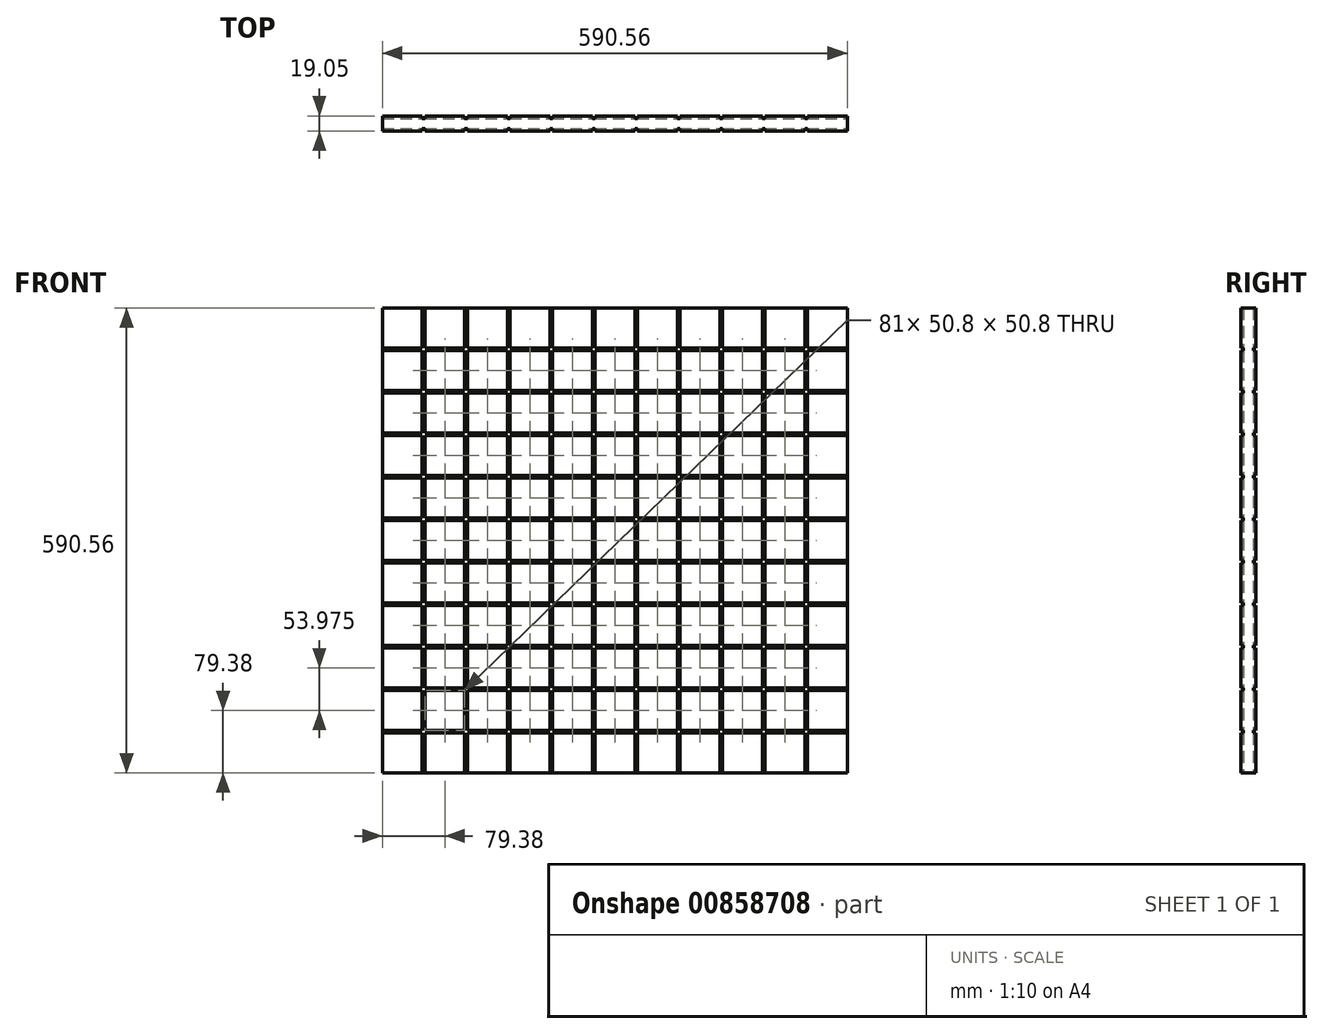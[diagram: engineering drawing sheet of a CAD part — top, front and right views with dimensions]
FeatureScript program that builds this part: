
annotation { "Feature Type Name" : "Feature", "Feature Type Description" : "" }
export const myFeature = defineFeature(function(context is Context, id is Id, definition is map)
    precondition{}
    {
        {
            var Q0;
            Q0=qCreatedBy(makeId("Front.planeOp"),FACE);
            var sketch = newSketch(context, id + "F0", { "sketchPlane" : qUnion([Q0])});
            skLineSegment(sketch, "E0.bottom", {"start": v(295.27, 295.28) * mm, "end": v(-295.27, 295.28) * mm});
            skLineSegment(sketch, "E0.top", {"start": v(295.27, -295.28) * mm, "end": v(-295.27, -295.28) * mm});
            skLineSegment(sketch, "E0.left", {"start": v(295.28, 295.27) * mm, "end": v(295.28, -295.28) * mm});
            skLineSegment(sketch, "E0.right", {"start": v(-295.28, 295.27) * mm, "end": v(-295.28, -295.27) * mm});
            skPoint(sketch, "E0.middle", {"position": v(0, 0) * mm});
            skSolve(sketch);
        }
        {
            var Q0;
            Q0=makeQuery(id+"F0.imprint","IMPRINT",FACE,{"disambiguationData":[TD([[makeQuery(id+"F0.imprint","IMPRINT",EDGE,{"derivedFrom":sQuery(id+"F0.wireOp",EDGE,"E0.bottom")}),1.0]])]});
            extrude(context, id + "F1", {"entities" : qUnion([Q0]), "depth" : 19.05 * mm, "offsetDistance" : 25.4 * mm});
        }
        {
            var Q0;
            Q0=makeQuery(id+"F1.opExtrude","CAP_FACE",FACE,{"disambiguationData":[OSD([sQuery(id+"F0.wireOp",EDGE,"E0.bottom"),sQuery(id+"F0.wireOp",EDGE,"E0.top"),sQuery(id+"F0.wireOp",EDGE,"E0.left"),sQuery(id+"F0.wireOp",EDGE,"E0.right")])],"isStart":false});
            var sketch = newSketch(context, id + "F2", { "sketchPlane" : qUnion([Q0])});
            skLineSegment(sketch, "E1.bottom", {"start": v(-244.48, 295.28) * mm, "end": v(-241.3, 295.28) * mm});
            skLineSegment(sketch, "E1.top", {"start": v(-244.47, -295.28) * mm, "end": v(-241.3, -295.28) * mm});
            skLineSegment(sketch, "E1.left", {"start": v(-244.48, 295.28) * mm, "end": v(-244.47, -295.28) * mm});
            skLineSegment(sketch, "E1.right", {"start": v(-241.3, 295.28) * mm, "end": v(-241.3, -295.28) * mm});
            skLineSegment(sketch, "E2.1.0.0", {"start": v(-190.5, 295.28) * mm, "end": v(-190.5, -295.28) * mm});
            skLineSegment(sketch, "E2.1.0.1", {"start": v(-187.32, 295.28) * mm, "end": v(-187.32, -295.28) * mm});
            skLineSegment(sketch, "E2.1.0.2", {"start": v(-190.5, 295.28) * mm, "end": v(-187.32, 295.28) * mm});
            skLineSegment(sketch, "E2.2.0.0", {"start": v(-136.52, 295.28) * mm, "end": v(-136.53, -295.28) * mm});
            skLineSegment(sketch, "E2.2.0.1", {"start": v(-133.35, 295.28) * mm, "end": v(-133.35, -295.28) * mm});
            skLineSegment(sketch, "E2.2.0.2", {"start": v(-136.52, 295.28) * mm, "end": v(-133.35, 295.28) * mm});
            skLineSegment(sketch, "E2.direction1", {"start": v(-244.47, -295.28) * mm, "end": v(-190.5, -295.28) * mm, "construction": true});
            skLineSegment(sketch, "E3.1.0.0", {"start": v(-190.5, -295.28) * mm, "end": v(-187.32, -295.28) * mm});
            skLineSegment(sketch, "E3.2.0.0", {"start": v(-136.52, -295.28) * mm, "end": v(-133.35, -295.28) * mm});
            skLineSegment(sketch, "E4.0.3.0", {"start": v(-82.55, -295.28) * mm, "end": v(-79.38, -295.28) * mm});
            skLineSegment(sketch, "E4.0.4.0", {"start": v(-28.57, -295.28) * mm, "end": v(-25.4, -295.28) * mm});
            skLineSegment(sketch, "E4.0.5.0", {"start": v(25.4, -295.28) * mm, "end": v(28.57, -295.28) * mm});
            skLineSegment(sketch, "E4.0.6.0", {"start": v(79.38, -295.28) * mm, "end": v(82.55, -295.28) * mm});
            skLineSegment(sketch, "E4.0.7.0", {"start": v(133.35, -295.28) * mm, "end": v(136.52, -295.28) * mm});
            skLineSegment(sketch, "E4.0.8.0", {"start": v(187.32, -295.28) * mm, "end": v(190.5, -295.28) * mm});
            skLineSegment(sketch, "E4.0.9.0", {"start": v(241.3, -295.28) * mm, "end": v(244.47, -295.28) * mm});
            skLineSegment(sketch, "E5.0.3.0", {"start": v(-82.55, 295.28) * mm, "end": v(-82.55, -295.28) * mm});
            skLineSegment(sketch, "E5.3.3.0", {"start": v(-79.37, 295.28) * mm, "end": v(-79.37, -295.28) * mm});
            skLineSegment(sketch, "E5.6.3.0", {"start": v(-82.55, 295.28) * mm, "end": v(-79.37, 295.28) * mm});
            skLineSegment(sketch, "E5.0.4.0", {"start": v(-28.57, 295.28) * mm, "end": v(-28.57, -295.28) * mm});
            skLineSegment(sketch, "E5.3.4.0", {"start": v(-25.4, 295.28) * mm, "end": v(-25.4, -295.28) * mm});
            skLineSegment(sketch, "E5.6.4.0", {"start": v(-28.57, 295.28) * mm, "end": v(-25.4, 295.28) * mm});
            skLineSegment(sketch, "E5.0.5.0", {"start": v(25.4, 295.28) * mm, "end": v(25.4, -295.28) * mm});
            skLineSegment(sketch, "E5.3.5.0", {"start": v(28.58, 295.28) * mm, "end": v(28.58, -295.28) * mm});
            skLineSegment(sketch, "E5.6.5.0", {"start": v(25.4, 295.28) * mm, "end": v(28.58, 295.28) * mm});
            skLineSegment(sketch, "E5.0.6.0", {"start": v(79.38, 295.28) * mm, "end": v(79.38, -295.28) * mm});
            skLineSegment(sketch, "E5.3.6.0", {"start": v(82.55, 295.28) * mm, "end": v(82.55, -295.28) * mm});
            skLineSegment(sketch, "E5.6.6.0", {"start": v(79.38, 295.28) * mm, "end": v(82.55, 295.28) * mm});
            skLineSegment(sketch, "E5.0.7.0", {"start": v(133.35, 295.28) * mm, "end": v(133.35, -295.28) * mm});
            skLineSegment(sketch, "E5.3.7.0", {"start": v(136.53, 295.28) * mm, "end": v(136.53, -295.28) * mm});
            skLineSegment(sketch, "E5.6.7.0", {"start": v(133.35, 295.28) * mm, "end": v(136.53, 295.28) * mm});
            skLineSegment(sketch, "E5.0.8.0", {"start": v(187.33, 295.28) * mm, "end": v(187.33, -295.28) * mm});
            skLineSegment(sketch, "E5.3.8.0", {"start": v(190.5, 295.28) * mm, "end": v(190.5, -295.28) * mm});
            skLineSegment(sketch, "E5.6.8.0", {"start": v(187.33, 295.28) * mm, "end": v(190.5, 295.28) * mm});
            skLineSegment(sketch, "E5.0.9.0", {"start": v(241.3, 295.28) * mm, "end": v(241.3, -295.28) * mm});
            skLineSegment(sketch, "E5.3.9.0", {"start": v(244.48, 295.28) * mm, "end": v(244.48, -295.28) * mm});
            skLineSegment(sketch, "E5.6.9.0", {"start": v(241.3, 295.28) * mm, "end": v(244.48, 295.28) * mm});
            skSolve(sketch);
        }
        {
            var Q0;
            Q0=qSketchRegion(id+"F2",true);
            extrude(context, id + "F3", {"entities" : qUnion([Q0]), "operationType" : NewBodyOperationType.REMOVE, "oppositeDirection" : true, "depth" : 3.17 * mm, "offsetDistance" : 25.4 * mm});
        }
        {
            var Q0;
            {var subQ0=sQuery(id+"F0.wireOp",EDGE,"E0.bottom");var subQ1=sQuery(id+"F0.wireOp",EDGE,"E0.right");var subQ2=sQuery(id+"F0.wireOp",EDGE,"E0.top");Q0=makeQuery(id+"F3.boolean.opBoolean","SPLIT",FACE,{"disambiguationData":[TD([makeQuery(id+"F1.opExtrude","SWEPT_FACE",FACE,{"disambiguationData":[OSD([subQ1])]})])],"derivedFrom":makeQuery(id+"F1.opExtrude","CAP_FACE",FACE,{"disambiguationData":[OSD([subQ0,subQ2,sQuery(id+"F0.wireOp",EDGE,"E0.left"),subQ1])],"isStart":false})});}
            var sketch = newSketch(context, id + "F4", { "sketchPlane" : qUnion([Q0])});
            skLineSegment(sketch, "E6.bottom", {"start": v(-295.27, 244.47) * mm, "end": v(295.28, 244.47) * mm});
            skLineSegment(sketch, "E6.top", {"start": v(-295.27, 241.3) * mm, "end": v(295.28, 241.3) * mm});
            skLineSegment(sketch, "E6.left", {"start": v(-295.28, 244.47) * mm, "end": v(-295.28, 241.3) * mm});
            skLineSegment(sketch, "E6.right", {"start": v(295.28, 244.47) * mm, "end": v(295.28, 241.3) * mm});
            skLineSegment(sketch, "E7.0.1.0", {"start": v(-295.28, 190.5) * mm, "end": v(-295.28, 187.33) * mm});
            skLineSegment(sketch, "E7.0.1.1", {"start": v(-295.27, 190.5) * mm, "end": v(295.28, 190.5) * mm});
            skLineSegment(sketch, "E7.0.1.2", {"start": v(-295.27, 187.32) * mm, "end": v(295.28, 187.32) * mm});
            skLineSegment(sketch, "E7.0.1.3", {"start": v(295.28, 190.5) * mm, "end": v(295.28, 187.32) * mm});
            skLineSegment(sketch, "E7.0.2.0", {"start": v(-295.28, 136.53) * mm, "end": v(-295.28, 133.35) * mm});
            skLineSegment(sketch, "E7.0.2.1", {"start": v(-295.27, 136.53) * mm, "end": v(295.28, 136.53) * mm});
            skLineSegment(sketch, "E7.0.2.2", {"start": v(-295.27, 133.35) * mm, "end": v(295.28, 133.35) * mm});
            skLineSegment(sketch, "E7.0.2.3", {"start": v(295.28, 136.53) * mm, "end": v(295.28, 133.35) * mm});
            skLineSegment(sketch, "E7.0.3.0", {"start": v(-295.28, 82.55) * mm, "end": v(-295.28, 79.38) * mm});
            skLineSegment(sketch, "E7.0.3.1", {"start": v(-295.27, 82.55) * mm, "end": v(295.28, 82.55) * mm});
            skLineSegment(sketch, "E7.0.3.2", {"start": v(-295.27, 79.38) * mm, "end": v(295.28, 79.38) * mm});
            skLineSegment(sketch, "E7.0.3.3", {"start": v(295.28, 82.55) * mm, "end": v(295.28, 79.38) * mm});
            skLineSegment(sketch, "E7.0.4.0", {"start": v(-295.28, 28.58) * mm, "end": v(-295.28, 25.4) * mm});
            skLineSegment(sketch, "E7.0.4.1", {"start": v(-295.27, 28.58) * mm, "end": v(295.28, 28.58) * mm});
            skLineSegment(sketch, "E7.0.4.2", {"start": v(-295.27, 25.4) * mm, "end": v(295.28, 25.4) * mm});
            skLineSegment(sketch, "E7.0.4.3", {"start": v(295.28, 28.58) * mm, "end": v(295.28, 25.4) * mm});
            skLineSegment(sketch, "E7.0.5.0", {"start": v(-295.28, -25.4) * mm, "end": v(-295.28, -28.57) * mm});
            skLineSegment(sketch, "E7.0.5.1", {"start": v(-295.27, -25.4) * mm, "end": v(295.28, -25.4) * mm});
            skLineSegment(sketch, "E7.0.5.2", {"start": v(-295.27, -28.57) * mm, "end": v(295.28, -28.57) * mm});
            skLineSegment(sketch, "E7.0.5.3", {"start": v(295.28, -25.4) * mm, "end": v(295.28, -28.57) * mm});
            skLineSegment(sketch, "E7.0.6.0", {"start": v(-295.28, -79.37) * mm, "end": v(-295.28, -82.55) * mm});
            skLineSegment(sketch, "E7.0.6.1", {"start": v(-295.27, -79.37) * mm, "end": v(295.28, -79.37) * mm});
            skLineSegment(sketch, "E7.0.6.2", {"start": v(-295.27, -82.55) * mm, "end": v(295.28, -82.55) * mm});
            skLineSegment(sketch, "E7.0.6.3", {"start": v(295.28, -79.37) * mm, "end": v(295.28, -82.55) * mm});
            skLineSegment(sketch, "E7.0.7.0", {"start": v(-295.28, -133.35) * mm, "end": v(-295.28, -136.52) * mm});
            skLineSegment(sketch, "E7.0.7.1", {"start": v(-295.27, -133.35) * mm, "end": v(295.28, -133.35) * mm});
            skLineSegment(sketch, "E7.0.7.2", {"start": v(-295.27, -136.52) * mm, "end": v(295.28, -136.52) * mm});
            skLineSegment(sketch, "E7.0.7.3", {"start": v(295.28, -133.35) * mm, "end": v(295.28, -136.52) * mm});
            skLineSegment(sketch, "E7.0.8.0", {"start": v(-295.28, -187.32) * mm, "end": v(-295.28, -190.5) * mm});
            skLineSegment(sketch, "E7.0.8.1", {"start": v(-295.27, -187.32) * mm, "end": v(295.28, -187.32) * mm});
            skLineSegment(sketch, "E7.0.8.2", {"start": v(-295.27, -190.5) * mm, "end": v(295.28, -190.5) * mm});
            skLineSegment(sketch, "E7.0.8.3", {"start": v(295.28, -187.32) * mm, "end": v(295.28, -190.5) * mm});
            skLineSegment(sketch, "E7.0.9.0", {"start": v(-295.28, -241.3) * mm, "end": v(-295.28, -244.47) * mm});
            skLineSegment(sketch, "E7.0.9.1", {"start": v(-295.27, -241.3) * mm, "end": v(295.28, -241.3) * mm});
            skLineSegment(sketch, "E7.0.9.2", {"start": v(-295.27, -244.47) * mm, "end": v(295.28, -244.47) * mm});
            skLineSegment(sketch, "E7.0.9.3", {"start": v(295.28, -241.3) * mm, "end": v(295.28, -244.47) * mm});
            skLineSegment(sketch, "E7.1.1.0", {"start": v(-295.28, 190.5) * mm, "end": v(-295.28, 187.33) * mm});
            skLineSegment(sketch, "E7.1.1.1", {"start": v(-295.27, 190.5) * mm, "end": v(295.28, 190.5) * mm});
            skLineSegment(sketch, "E7.1.1.2", {"start": v(-295.27, 187.32) * mm, "end": v(295.28, 187.32) * mm});
            skLineSegment(sketch, "E7.1.1.3", {"start": v(295.28, 190.5) * mm, "end": v(295.28, 187.32) * mm});
            skLineSegment(sketch, "E7.1.2.0", {"start": v(-295.28, 136.53) * mm, "end": v(-295.28, 133.35) * mm});
            skLineSegment(sketch, "E7.1.2.1", {"start": v(-295.27, 136.53) * mm, "end": v(295.28, 136.53) * mm});
            skLineSegment(sketch, "E7.1.2.2", {"start": v(-295.27, 133.35) * mm, "end": v(295.28, 133.35) * mm});
            skLineSegment(sketch, "E7.1.2.3", {"start": v(295.28, 136.53) * mm, "end": v(295.28, 133.35) * mm});
            skLineSegment(sketch, "E7.1.3.0", {"start": v(-295.28, 82.55) * mm, "end": v(-295.28, 79.38) * mm});
            skLineSegment(sketch, "E7.1.3.1", {"start": v(-295.27, 82.55) * mm, "end": v(295.28, 82.55) * mm});
            skLineSegment(sketch, "E7.1.3.2", {"start": v(-295.27, 79.38) * mm, "end": v(295.28, 79.38) * mm});
            skLineSegment(sketch, "E7.1.3.3", {"start": v(295.28, 82.55) * mm, "end": v(295.28, 79.38) * mm});
            skLineSegment(sketch, "E7.1.4.0", {"start": v(-295.28, 28.58) * mm, "end": v(-295.28, 25.4) * mm});
            skLineSegment(sketch, "E7.1.4.1", {"start": v(-295.27, 28.58) * mm, "end": v(295.28, 28.58) * mm});
            skLineSegment(sketch, "E7.1.4.2", {"start": v(-295.27, 25.4) * mm, "end": v(295.28, 25.4) * mm});
            skLineSegment(sketch, "E7.1.4.3", {"start": v(295.28, 28.58) * mm, "end": v(295.28, 25.4) * mm});
            skLineSegment(sketch, "E7.1.5.0", {"start": v(-295.28, -25.4) * mm, "end": v(-295.28, -28.57) * mm});
            skLineSegment(sketch, "E7.1.5.1", {"start": v(-295.27, -25.4) * mm, "end": v(295.28, -25.4) * mm});
            skLineSegment(sketch, "E7.1.5.2", {"start": v(-295.27, -28.57) * mm, "end": v(295.28, -28.57) * mm});
            skLineSegment(sketch, "E7.1.5.3", {"start": v(295.28, -25.4) * mm, "end": v(295.28, -28.57) * mm});
            skLineSegment(sketch, "E7.1.6.0", {"start": v(-295.28, -79.37) * mm, "end": v(-295.28, -82.55) * mm});
            skLineSegment(sketch, "E7.1.6.1", {"start": v(-295.27, -79.37) * mm, "end": v(295.28, -79.37) * mm});
            skLineSegment(sketch, "E7.1.6.2", {"start": v(-295.27, -82.55) * mm, "end": v(295.28, -82.55) * mm});
            skLineSegment(sketch, "E7.1.6.3", {"start": v(295.28, -79.37) * mm, "end": v(295.28, -82.55) * mm});
            skLineSegment(sketch, "E7.1.7.0", {"start": v(-295.28, -133.35) * mm, "end": v(-295.28, -136.52) * mm});
            skLineSegment(sketch, "E7.1.7.1", {"start": v(-295.27, -133.35) * mm, "end": v(295.28, -133.35) * mm});
            skLineSegment(sketch, "E7.1.7.2", {"start": v(-295.27, -136.52) * mm, "end": v(295.28, -136.52) * mm});
            skLineSegment(sketch, "E7.1.7.3", {"start": v(295.28, -133.35) * mm, "end": v(295.28, -136.52) * mm});
            skLineSegment(sketch, "E7.1.8.0", {"start": v(-295.28, -187.32) * mm, "end": v(-295.28, -190.5) * mm});
            skLineSegment(sketch, "E7.1.8.1", {"start": v(-295.27, -187.32) * mm, "end": v(295.28, -187.32) * mm});
            skLineSegment(sketch, "E7.1.8.2", {"start": v(-295.27, -190.5) * mm, "end": v(295.28, -190.5) * mm});
            skLineSegment(sketch, "E7.1.8.3", {"start": v(295.28, -187.32) * mm, "end": v(295.28, -190.5) * mm});
            skLineSegment(sketch, "E7.1.9.0", {"start": v(-295.28, -241.3) * mm, "end": v(-295.28, -244.47) * mm});
            skLineSegment(sketch, "E7.1.9.1", {"start": v(-295.27, -241.3) * mm, "end": v(295.28, -241.3) * mm});
            skLineSegment(sketch, "E7.1.9.2", {"start": v(-295.27, -244.47) * mm, "end": v(295.28, -244.47) * mm});
            skLineSegment(sketch, "E7.1.9.3", {"start": v(295.28, -241.3) * mm, "end": v(295.28, -244.47) * mm});
            skLineSegment(sketch, "E7.2.1.0", {"start": v(-295.28, 190.5) * mm, "end": v(-295.28, 187.33) * mm});
            skLineSegment(sketch, "E7.2.1.1", {"start": v(-295.27, 190.5) * mm, "end": v(295.28, 190.5) * mm});
            skLineSegment(sketch, "E7.2.1.2", {"start": v(-295.27, 187.32) * mm, "end": v(295.28, 187.32) * mm});
            skLineSegment(sketch, "E7.2.1.3", {"start": v(295.28, 190.5) * mm, "end": v(295.28, 187.32) * mm});
            skLineSegment(sketch, "E7.2.2.0", {"start": v(-295.28, 136.53) * mm, "end": v(-295.28, 133.35) * mm});
            skLineSegment(sketch, "E7.2.2.1", {"start": v(-295.27, 136.53) * mm, "end": v(295.28, 136.53) * mm});
            skLineSegment(sketch, "E7.2.2.2", {"start": v(-295.27, 133.35) * mm, "end": v(295.28, 133.35) * mm});
            skLineSegment(sketch, "E7.2.2.3", {"start": v(295.28, 136.53) * mm, "end": v(295.28, 133.35) * mm});
            skLineSegment(sketch, "E7.2.3.0", {"start": v(-295.28, 82.55) * mm, "end": v(-295.28, 79.38) * mm});
            skLineSegment(sketch, "E7.2.3.1", {"start": v(-295.27, 82.55) * mm, "end": v(295.28, 82.55) * mm});
            skLineSegment(sketch, "E7.2.3.2", {"start": v(-295.27, 79.38) * mm, "end": v(295.28, 79.38) * mm});
            skLineSegment(sketch, "E7.2.3.3", {"start": v(295.28, 82.55) * mm, "end": v(295.28, 79.38) * mm});
            skLineSegment(sketch, "E7.2.4.0", {"start": v(-295.28, 28.58) * mm, "end": v(-295.28, 25.4) * mm});
            skLineSegment(sketch, "E7.2.4.1", {"start": v(-295.27, 28.58) * mm, "end": v(295.28, 28.58) * mm});
            skLineSegment(sketch, "E7.2.4.2", {"start": v(-295.27, 25.4) * mm, "end": v(295.28, 25.4) * mm});
            skLineSegment(sketch, "E7.2.4.3", {"start": v(295.28, 28.58) * mm, "end": v(295.28, 25.4) * mm});
            skLineSegment(sketch, "E7.2.5.0", {"start": v(-295.28, -25.4) * mm, "end": v(-295.28, -28.57) * mm});
            skLineSegment(sketch, "E7.2.5.1", {"start": v(-295.27, -25.4) * mm, "end": v(295.28, -25.4) * mm});
            skLineSegment(sketch, "E7.2.5.2", {"start": v(-295.27, -28.57) * mm, "end": v(295.28, -28.57) * mm});
            skLineSegment(sketch, "E7.2.5.3", {"start": v(295.28, -25.4) * mm, "end": v(295.28, -28.57) * mm});
            skLineSegment(sketch, "E7.2.6.0", {"start": v(-295.28, -79.37) * mm, "end": v(-295.28, -82.55) * mm});
            skLineSegment(sketch, "E7.2.6.1", {"start": v(-295.27, -79.37) * mm, "end": v(295.28, -79.37) * mm});
            skLineSegment(sketch, "E7.2.6.2", {"start": v(-295.27, -82.55) * mm, "end": v(295.28, -82.55) * mm});
            skLineSegment(sketch, "E7.2.6.3", {"start": v(295.28, -79.37) * mm, "end": v(295.28, -82.55) * mm});
            skLineSegment(sketch, "E7.2.7.0", {"start": v(-295.28, -133.35) * mm, "end": v(-295.28, -136.52) * mm});
            skLineSegment(sketch, "E7.2.7.1", {"start": v(-295.27, -133.35) * mm, "end": v(295.28, -133.35) * mm});
            skLineSegment(sketch, "E7.2.7.2", {"start": v(-295.27, -136.52) * mm, "end": v(295.28, -136.52) * mm});
            skLineSegment(sketch, "E7.2.7.3", {"start": v(295.28, -133.35) * mm, "end": v(295.28, -136.52) * mm});
            skLineSegment(sketch, "E7.2.8.0", {"start": v(-295.28, -187.32) * mm, "end": v(-295.28, -190.5) * mm});
            skLineSegment(sketch, "E7.2.8.1", {"start": v(-295.27, -187.32) * mm, "end": v(295.28, -187.32) * mm});
            skLineSegment(sketch, "E7.2.8.2", {"start": v(-295.27, -190.5) * mm, "end": v(295.28, -190.5) * mm});
            skLineSegment(sketch, "E7.2.8.3", {"start": v(295.28, -187.32) * mm, "end": v(295.28, -190.5) * mm});
            skLineSegment(sketch, "E7.2.9.0", {"start": v(-295.28, -241.3) * mm, "end": v(-295.28, -244.47) * mm});
            skLineSegment(sketch, "E7.2.9.1", {"start": v(-295.27, -241.3) * mm, "end": v(295.28, -241.3) * mm});
            skLineSegment(sketch, "E7.2.9.2", {"start": v(-295.27, -244.47) * mm, "end": v(295.28, -244.47) * mm});
            skLineSegment(sketch, "E7.2.9.3", {"start": v(295.28, -241.3) * mm, "end": v(295.28, -244.47) * mm});
            skLineSegment(sketch, "E7.direction1", {"start": v(-295.28, 241.3) * mm, "end": v(-295.28, 241.3) * mm});
            skLineSegment(sketch, "E7.direction2", {"start": v(-295.28, 241.3) * mm, "end": v(-295.28, 187.33) * mm, "construction": true});
            skSolve(sketch);
        }
        {
            var Q0;
            Q0=qSketchRegion(id+"F4",true);
            extrude(context, id + "F5", {"entities" : qUnion([Q0]), "operationType" : NewBodyOperationType.REMOVE, "oppositeDirection" : true, "depth" : 3.17 * mm, "offsetDistance" : 25.4 * mm});
        }
        {
            var Q0;
            Q0=makeQuery(id+"F1.opExtrude","CAP_FACE",FACE,{"disambiguationData":[OSD([sQuery(id+"F0.wireOp",EDGE,"E0.bottom"),sQuery(id+"F0.wireOp",EDGE,"E0.top"),sQuery(id+"F0.wireOp",EDGE,"E0.left"),sQuery(id+"F0.wireOp",EDGE,"E0.right")])],"isStart":true});
            var sketch = newSketch(context, id + "F6", { "sketchPlane" : qUnion([Q0])});
            skLineSegment(sketch, "E8.0", {"start": v(244.48, 295.28) * mm, "end": v(241.3, 295.28) * mm});
            skLineSegment(sketch, "E8.1", {"start": v(244.47, -295.28) * mm, "end": v(241.3, -295.28) * mm});
            skLineSegment(sketch, "E8.2", {"start": v(244.48, 295.28) * mm, "end": v(244.47, -295.28) * mm});
            skLineSegment(sketch, "E8.3", {"start": v(241.3, 295.28) * mm, "end": v(241.3, -295.28) * mm});
            skLineSegment(sketch, "E8.4", {"start": v(190.5, 295.28) * mm, "end": v(190.5, -295.28) * mm});
            skLineSegment(sketch, "E8.5", {"start": v(187.32, 295.28) * mm, "end": v(187.32, -295.28) * mm});
            skLineSegment(sketch, "E8.6", {"start": v(190.5, 295.28) * mm, "end": v(187.32, 295.28) * mm});
            skLineSegment(sketch, "E8.7", {"start": v(136.52, 295.28) * mm, "end": v(136.53, -295.28) * mm});
            skLineSegment(sketch, "E8.8", {"start": v(133.35, 295.28) * mm, "end": v(133.35, -295.28) * mm});
            skLineSegment(sketch, "E8.9", {"start": v(136.52, 295.28) * mm, "end": v(133.35, 295.28) * mm});
            skLineSegment(sketch, "E8.10", {"start": v(244.47, -295.28) * mm, "end": v(190.5, -295.28) * mm});
            skLineSegment(sketch, "E8.11", {"start": v(190.5, -295.28) * mm, "end": v(187.32, -295.28) * mm});
            skLineSegment(sketch, "E8.12", {"start": v(136.52, -295.28) * mm, "end": v(133.35, -295.28) * mm});
            skLineSegment(sketch, "E8.13", {"start": v(244.47, -295.28) * mm, "end": v(190.5, -295.28) * mm});
            skLineSegment(sketch, "E8.14", {"start": v(82.55, -295.28) * mm, "end": v(79.38, -295.28) * mm});
            skLineSegment(sketch, "E8.15", {"start": v(28.57, -295.28) * mm, "end": v(25.4, -295.28) * mm});
            skLineSegment(sketch, "E8.16", {"start": v(-25.4, -295.28) * mm, "end": v(-28.57, -295.28) * mm});
            skLineSegment(sketch, "E8.17", {"start": v(-79.38, -295.28) * mm, "end": v(-82.55, -295.28) * mm});
            skLineSegment(sketch, "E8.18", {"start": v(-133.35, -295.28) * mm, "end": v(-136.52, -295.28) * mm});
            skLineSegment(sketch, "E8.19", {"start": v(-187.32, -295.28) * mm, "end": v(-190.5, -295.28) * mm});
            skLineSegment(sketch, "E8.20", {"start": v(-241.3, -295.28) * mm, "end": v(-244.47, -295.28) * mm});
            skLineSegment(sketch, "E8.21", {"start": v(82.55, 295.28) * mm, "end": v(82.55, -295.28) * mm});
            skLineSegment(sketch, "E8.22", {"start": v(79.37, 295.28) * mm, "end": v(79.37, -295.28) * mm});
            skLineSegment(sketch, "E8.23", {"start": v(82.55, 295.28) * mm, "end": v(79.37, 295.28) * mm});
            skLineSegment(sketch, "E8.24", {"start": v(28.57, 295.28) * mm, "end": v(28.57, -295.28) * mm});
            skLineSegment(sketch, "E8.25", {"start": v(25.4, 295.28) * mm, "end": v(25.4, -295.28) * mm});
            skLineSegment(sketch, "E8.26", {"start": v(28.57, 295.28) * mm, "end": v(25.4, 295.28) * mm});
            skLineSegment(sketch, "E8.27", {"start": v(-25.4, 295.28) * mm, "end": v(-25.4, -295.28) * mm});
            skLineSegment(sketch, "E8.28", {"start": v(-28.58, 295.28) * mm, "end": v(-28.58, -295.28) * mm});
            skLineSegment(sketch, "E8.29", {"start": v(-25.4, 295.28) * mm, "end": v(-28.58, 295.28) * mm});
            skLineSegment(sketch, "E8.30", {"start": v(-79.38, 295.28) * mm, "end": v(-79.38, -295.28) * mm});
            skLineSegment(sketch, "E8.31", {"start": v(-82.55, 295.28) * mm, "end": v(-82.55, -295.28) * mm});
            skLineSegment(sketch, "E8.32", {"start": v(-79.38, 295.28) * mm, "end": v(-82.55, 295.28) * mm});
            skLineSegment(sketch, "E8.33", {"start": v(-133.35, 295.28) * mm, "end": v(-133.35, -295.28) * mm});
            skLineSegment(sketch, "E8.34", {"start": v(-136.53, 295.28) * mm, "end": v(-136.53, -295.28) * mm});
            skLineSegment(sketch, "E8.35", {"start": v(-133.35, 295.28) * mm, "end": v(-136.53, 295.28) * mm});
            skLineSegment(sketch, "E8.36", {"start": v(-187.33, 295.28) * mm, "end": v(-187.33, -295.28) * mm});
            skLineSegment(sketch, "E8.37", {"start": v(-190.5, 295.28) * mm, "end": v(-190.5, -295.28) * mm});
            skLineSegment(sketch, "E8.38", {"start": v(-187.33, 295.28) * mm, "end": v(-190.5, 295.28) * mm});
            skLineSegment(sketch, "E8.39", {"start": v(-241.3, 295.28) * mm, "end": v(-241.3, -295.28) * mm});
            skLineSegment(sketch, "E8.40", {"start": v(-244.48, 295.28) * mm, "end": v(-244.48, -295.28) * mm});
            skLineSegment(sketch, "E8.41", {"start": v(-241.3, 295.28) * mm, "end": v(-244.48, 295.28) * mm});
            skSolve(sketch);
        }
        {
            var Q0;
            Q0 = qSketchRegion(id + "F6", true);
            extrude(context, id + "F7", {"entities" : qUnion([Q0]), "operationType" : NewBodyOperationType.REMOVE, "oppositeDirection" : true, "depth" : 3.17 * mm, "offsetDistance" : 25.4 * mm});
        }
        {
            var Q0;
            Q0=makeQuery(id+"F0.imprint","IMPRINT",FACE,{"disambiguationData":[TD([[makeQuery(id+"F0.imprint","IMPRINT",EDGE,{"derivedFrom":sQuery(id+"F0.wireOp",EDGE,"E0.bottom")}),1.0]])]});
            var sketch = newSketch(context, id + "F8", { "sketchPlane" : qUnion([Q0])});
            skLineSegment(sketch, "E9.1", {"start": v(-295.27, 244.47) * mm, "end": v(295.28, 244.47) * mm});
            skLineSegment(sketch, "E9.2", {"start": v(-295.27, 241.3) * mm, "end": v(295.28, 241.3) * mm, "construction": true});
            skLineSegment(sketch, "E9.3", {"start": v(-295.28, 244.47) * mm, "end": v(-295.28, 241.3) * mm});
            skLineSegment(sketch, "E9.4", {"start": v(295.28, 244.47) * mm, "end": v(295.28, 241.3) * mm});
            skLineSegment(sketch, "E9.5", {"start": v(-295.28, 190.5) * mm, "end": v(-295.28, 187.33) * mm});
            skLineSegment(sketch, "E9.6", {"start": v(-295.27, 190.5) * mm, "end": v(295.28, 190.5) * mm});
            skLineSegment(sketch, "E9.7", {"start": v(-295.27, 187.32) * mm, "end": v(295.28, 187.32) * mm});
            skLineSegment(sketch, "E9.8", {"start": v(295.28, 190.5) * mm, "end": v(295.28, 187.32) * mm});
            skLineSegment(sketch, "E9.9", {"start": v(-295.28, 136.53) * mm, "end": v(-295.28, 133.35) * mm});
            skLineSegment(sketch, "E9.10", {"start": v(-295.27, 136.53) * mm, "end": v(295.28, 136.53) * mm});
            skLineSegment(sketch, "E9.11", {"start": v(-295.27, 133.35) * mm, "end": v(295.28, 133.35) * mm});
            skLineSegment(sketch, "E9.12", {"start": v(295.28, 136.53) * mm, "end": v(295.28, 133.35) * mm});
            skLineSegment(sketch, "E9.13", {"start": v(-295.28, 82.55) * mm, "end": v(-295.28, 79.38) * mm});
            skLineSegment(sketch, "E9.14", {"start": v(-295.27, 82.55) * mm, "end": v(295.28, 82.55) * mm});
            skLineSegment(sketch, "E9.15", {"start": v(-295.27, 79.38) * mm, "end": v(295.28, 79.38) * mm});
            skLineSegment(sketch, "E9.16", {"start": v(295.28, 82.55) * mm, "end": v(295.28, 79.38) * mm});
            skLineSegment(sketch, "E9.17", {"start": v(-295.28, 28.58) * mm, "end": v(-295.28, 25.4) * mm});
            skLineSegment(sketch, "E9.18", {"start": v(-295.27, 28.58) * mm, "end": v(295.28, 28.58) * mm});
            skLineSegment(sketch, "E9.19", {"start": v(-295.27, 25.4) * mm, "end": v(295.28, 25.4) * mm});
            skLineSegment(sketch, "E9.20", {"start": v(295.28, 28.58) * mm, "end": v(295.28, 25.4) * mm});
            skLineSegment(sketch, "E9.21", {"start": v(-295.28, -25.4) * mm, "end": v(-295.28, -28.57) * mm});
            skLineSegment(sketch, "E9.22", {"start": v(-295.27, -25.4) * mm, "end": v(295.28, -25.4) * mm});
            skLineSegment(sketch, "E9.23", {"start": v(-295.27, -28.57) * mm, "end": v(295.28, -28.57) * mm});
            skLineSegment(sketch, "E9.24", {"start": v(295.28, -25.4) * mm, "end": v(295.28, -28.57) * mm});
            skLineSegment(sketch, "E9.25", {"start": v(-295.28, -79.37) * mm, "end": v(-295.28, -82.55) * mm});
            skLineSegment(sketch, "E9.26", {"start": v(-295.27, -79.37) * mm, "end": v(295.28, -79.37) * mm});
            skLineSegment(sketch, "E9.27", {"start": v(-295.27, -82.55) * mm, "end": v(295.28, -82.55) * mm});
            skLineSegment(sketch, "E9.28", {"start": v(295.28, -79.37) * mm, "end": v(295.28, -82.55) * mm});
            skLineSegment(sketch, "E9.29", {"start": v(-295.28, -133.35) * mm, "end": v(-295.28, -136.52) * mm});
            skLineSegment(sketch, "E9.30", {"start": v(-295.27, -133.35) * mm, "end": v(295.28, -133.35) * mm});
            skLineSegment(sketch, "E9.31", {"start": v(-295.27, -136.52) * mm, "end": v(295.28, -136.52) * mm});
            skLineSegment(sketch, "E9.32", {"start": v(295.28, -133.35) * mm, "end": v(295.28, -136.52) * mm});
            skLineSegment(sketch, "E9.33", {"start": v(-295.28, -187.32) * mm, "end": v(-295.28, -190.5) * mm});
            skLineSegment(sketch, "E9.34", {"start": v(-295.27, -187.32) * mm, "end": v(295.28, -187.32) * mm});
            skLineSegment(sketch, "E9.35", {"start": v(-295.27, -190.5) * mm, "end": v(295.28, -190.5) * mm});
            skLineSegment(sketch, "E9.36", {"start": v(295.28, -187.32) * mm, "end": v(295.28, -190.5) * mm});
            skLineSegment(sketch, "E9.37", {"start": v(-295.28, -241.3) * mm, "end": v(-295.28, -244.47) * mm});
            skLineSegment(sketch, "E9.38", {"start": v(-295.27, -241.3) * mm, "end": v(295.28, -241.3) * mm});
            skLineSegment(sketch, "E9.39", {"start": v(-295.27, -244.47) * mm, "end": v(295.28, -244.47) * mm});
            skLineSegment(sketch, "E9.40", {"start": v(295.28, -241.3) * mm, "end": v(295.28, -244.47) * mm});
            skLineSegment(sketch, "E9.41", {"start": v(-295.28, 244.47) * mm, "end": v(-295.28, 241.3) * mm});
            skLineSegment(sketch, "E9.42", {"start": v(-295.27, 244.47) * mm, "end": v(295.28, 244.47) * mm});
            skLineSegment(sketch, "E9.43", {"start": v(-295.27, 241.3) * mm, "end": v(295.28, 241.3) * mm});
            skLineSegment(sketch, "E9.44", {"start": v(295.28, 244.47) * mm, "end": v(295.28, 241.3) * mm});
            skLineSegment(sketch, "E9.45", {"start": v(-295.28, 190.5) * mm, "end": v(-295.28, 187.33) * mm});
            skLineSegment(sketch, "E9.46", {"start": v(-295.27, 190.5) * mm, "end": v(295.28, 190.5) * mm});
            skLineSegment(sketch, "E9.47", {"start": v(-295.27, 187.32) * mm, "end": v(295.28, 187.32) * mm});
            skLineSegment(sketch, "E9.48", {"start": v(295.28, 190.5) * mm, "end": v(295.28, 187.32) * mm});
            skLineSegment(sketch, "E9.49", {"start": v(-295.28, 136.53) * mm, "end": v(-295.28, 133.35) * mm});
            skLineSegment(sketch, "E9.50", {"start": v(-295.27, 136.53) * mm, "end": v(295.28, 136.53) * mm});
            skLineSegment(sketch, "E9.51", {"start": v(-295.27, 133.35) * mm, "end": v(295.28, 133.35) * mm});
            skLineSegment(sketch, "E9.52", {"start": v(295.28, 136.53) * mm, "end": v(295.28, 133.35) * mm});
            skLineSegment(sketch, "E9.53", {"start": v(-295.28, 82.55) * mm, "end": v(-295.28, 79.38) * mm});
            skLineSegment(sketch, "E9.54", {"start": v(-295.27, 82.55) * mm, "end": v(295.28, 82.55) * mm});
            skLineSegment(sketch, "E9.55", {"start": v(-295.27, 79.38) * mm, "end": v(295.28, 79.38) * mm});
            skLineSegment(sketch, "E9.56", {"start": v(295.28, 82.55) * mm, "end": v(295.28, 79.38) * mm});
            skLineSegment(sketch, "E9.57", {"start": v(-295.28, 28.58) * mm, "end": v(-295.28, 25.4) * mm});
            skLineSegment(sketch, "E9.58", {"start": v(-295.27, 28.58) * mm, "end": v(295.28, 28.58) * mm});
            skLineSegment(sketch, "E9.59", {"start": v(-295.27, 25.4) * mm, "end": v(295.28, 25.4) * mm});
            skLineSegment(sketch, "E9.60", {"start": v(295.28, 28.58) * mm, "end": v(295.28, 25.4) * mm});
            skLineSegment(sketch, "E9.61", {"start": v(-295.28, -25.4) * mm, "end": v(-295.28, -28.57) * mm});
            skLineSegment(sketch, "E9.62", {"start": v(-295.27, -25.4) * mm, "end": v(295.28, -25.4) * mm});
            skLineSegment(sketch, "E9.63", {"start": v(-295.27, -28.57) * mm, "end": v(295.28, -28.57) * mm});
            skLineSegment(sketch, "E9.64", {"start": v(295.28, -25.4) * mm, "end": v(295.28, -28.57) * mm});
            skLineSegment(sketch, "E9.65", {"start": v(-295.28, -79.37) * mm, "end": v(-295.28, -82.55) * mm});
            skLineSegment(sketch, "E9.66", {"start": v(-295.27, -79.37) * mm, "end": v(295.28, -79.37) * mm});
            skLineSegment(sketch, "E9.67", {"start": v(-295.27, -82.55) * mm, "end": v(295.28, -82.55) * mm});
            skLineSegment(sketch, "E9.68", {"start": v(295.28, -79.37) * mm, "end": v(295.28, -82.55) * mm});
            skLineSegment(sketch, "E9.69", {"start": v(-295.28, -133.35) * mm, "end": v(-295.28, -136.52) * mm});
            skLineSegment(sketch, "E9.70", {"start": v(-295.27, -133.35) * mm, "end": v(295.28, -133.35) * mm});
            skLineSegment(sketch, "E9.71", {"start": v(-295.27, -136.52) * mm, "end": v(295.28, -136.52) * mm});
            skLineSegment(sketch, "E9.72", {"start": v(295.28, -133.35) * mm, "end": v(295.28, -136.52) * mm});
            skLineSegment(sketch, "E9.73", {"start": v(-295.28, -187.32) * mm, "end": v(-295.28, -190.5) * mm});
            skLineSegment(sketch, "E9.74", {"start": v(-295.27, -187.32) * mm, "end": v(295.28, -187.32) * mm});
            skLineSegment(sketch, "E9.75", {"start": v(-295.27, -190.5) * mm, "end": v(295.28, -190.5) * mm});
            skLineSegment(sketch, "E9.76", {"start": v(295.28, -187.32) * mm, "end": v(295.28, -190.5) * mm});
            skLineSegment(sketch, "E9.77", {"start": v(-295.28, -241.3) * mm, "end": v(-295.28, -244.47) * mm});
            skLineSegment(sketch, "E9.78", {"start": v(-295.27, -241.3) * mm, "end": v(295.28, -241.3) * mm});
            skLineSegment(sketch, "E9.79", {"start": v(-295.27, -244.47) * mm, "end": v(295.28, -244.47) * mm});
            skLineSegment(sketch, "E9.80", {"start": v(295.28, -241.3) * mm, "end": v(295.28, -244.47) * mm});
            skLineSegment(sketch, "E9.81", {"start": v(-295.28, 244.47) * mm, "end": v(-295.28, 241.3) * mm});
            skLineSegment(sketch, "E9.82", {"start": v(-295.27, 244.47) * mm, "end": v(295.28, 244.47) * mm});
            skLineSegment(sketch, "E9.83", {"start": v(-295.27, 241.3) * mm, "end": v(295.28, 241.3) * mm});
            skLineSegment(sketch, "E9.84", {"start": v(295.28, 244.47) * mm, "end": v(295.28, 241.3) * mm});
            skLineSegment(sketch, "E9.85", {"start": v(-295.28, 190.5) * mm, "end": v(-295.28, 187.33) * mm});
            skLineSegment(sketch, "E9.86", {"start": v(-295.27, 190.5) * mm, "end": v(295.28, 190.5) * mm});
            skLineSegment(sketch, "E9.87", {"start": v(-295.27, 187.32) * mm, "end": v(295.28, 187.32) * mm});
            skLineSegment(sketch, "E9.88", {"start": v(295.28, 190.5) * mm, "end": v(295.28, 187.32) * mm});
            skLineSegment(sketch, "E9.89", {"start": v(-295.28, 136.53) * mm, "end": v(-295.28, 133.35) * mm});
            skLineSegment(sketch, "E9.90", {"start": v(-295.27, 136.53) * mm, "end": v(295.28, 136.53) * mm});
            skLineSegment(sketch, "E9.91", {"start": v(-295.27, 133.35) * mm, "end": v(295.28, 133.35) * mm});
            skLineSegment(sketch, "E9.92", {"start": v(295.28, 136.53) * mm, "end": v(295.28, 133.35) * mm});
            skLineSegment(sketch, "E9.93", {"start": v(-295.28, 82.55) * mm, "end": v(-295.28, 79.38) * mm});
            skLineSegment(sketch, "E9.94", {"start": v(-295.27, 82.55) * mm, "end": v(295.28, 82.55) * mm});
            skLineSegment(sketch, "E9.95", {"start": v(-295.27, 79.38) * mm, "end": v(295.28, 79.38) * mm});
            skLineSegment(sketch, "E9.96", {"start": v(295.28, 82.55) * mm, "end": v(295.28, 79.38) * mm});
            skLineSegment(sketch, "E9.97", {"start": v(-295.28, 28.58) * mm, "end": v(-295.28, 25.4) * mm});
            skLineSegment(sketch, "E9.98", {"start": v(-295.27, 28.58) * mm, "end": v(295.28, 28.58) * mm});
            skLineSegment(sketch, "E9.99", {"start": v(-295.27, 25.4) * mm, "end": v(295.28, 25.4) * mm});
            skLineSegment(sketch, "E9.100", {"start": v(295.28, 28.58) * mm, "end": v(295.28, 25.4) * mm});
            skLineSegment(sketch, "E9.101", {"start": v(-295.28, -25.4) * mm, "end": v(-295.28, -28.57) * mm});
            skLineSegment(sketch, "E9.102", {"start": v(-295.27, -25.4) * mm, "end": v(295.28, -25.4) * mm});
            skLineSegment(sketch, "E9.103", {"start": v(-295.27, -28.57) * mm, "end": v(295.28, -28.57) * mm});
            skLineSegment(sketch, "E9.104", {"start": v(295.28, -25.4) * mm, "end": v(295.28, -28.57) * mm});
            skLineSegment(sketch, "E9.105", {"start": v(-295.28, -79.37) * mm, "end": v(-295.28, -82.55) * mm});
            skLineSegment(sketch, "E9.106", {"start": v(-295.27, -79.37) * mm, "end": v(295.28, -79.37) * mm});
            skLineSegment(sketch, "E9.107", {"start": v(-295.27, -82.55) * mm, "end": v(295.28, -82.55) * mm});
            skLineSegment(sketch, "E9.108", {"start": v(295.28, -79.37) * mm, "end": v(295.28, -82.55) * mm});
            skLineSegment(sketch, "E9.109", {"start": v(-295.28, -133.35) * mm, "end": v(-295.28, -136.52) * mm});
            skLineSegment(sketch, "E9.110", {"start": v(-295.27, -133.35) * mm, "end": v(295.28, -133.35) * mm});
            skLineSegment(sketch, "E9.111", {"start": v(-295.27, -136.52) * mm, "end": v(295.28, -136.52) * mm});
            skLineSegment(sketch, "E9.112", {"start": v(295.28, -133.35) * mm, "end": v(295.28, -136.52) * mm});
            skLineSegment(sketch, "E9.113", {"start": v(-295.28, -187.32) * mm, "end": v(-295.28, -190.5) * mm});
            skLineSegment(sketch, "E9.114", {"start": v(-295.27, -187.32) * mm, "end": v(295.28, -187.32) * mm});
            skLineSegment(sketch, "E9.115", {"start": v(-295.27, -190.5) * mm, "end": v(295.28, -190.5) * mm});
            skLineSegment(sketch, "E9.116", {"start": v(295.28, -187.32) * mm, "end": v(295.28, -190.5) * mm});
            skLineSegment(sketch, "E9.117", {"start": v(-295.28, -241.3) * mm, "end": v(-295.28, -244.47) * mm});
            skLineSegment(sketch, "E9.118", {"start": v(-295.27, -241.3) * mm, "end": v(295.28, -241.3) * mm});
            skLineSegment(sketch, "E9.119", {"start": v(-295.27, -244.47) * mm, "end": v(295.28, -244.47) * mm});
            skLineSegment(sketch, "E9.120", {"start": v(295.28, -241.3) * mm, "end": v(295.28, -244.47) * mm});
            skPoint(sketch, "E9.121", {"position": v(-295.28, 241.3) * mm});
            skLineSegment(sketch, "E9.122", {"start": v(-295.28, 241.3) * mm, "end": v(-295.28, 187.33) * mm});
            skSolve(sketch);
        }
        {
            var Q0;
            Q0 = qSketchRegion(id + "F8", true);
            extrude(context, id + "F9", {"entities" : qUnion([Q0]), "operationType" : NewBodyOperationType.REMOVE, "depth" : 3.17 * mm, "offsetDistance" : 25.4 * mm});
        }
    });
